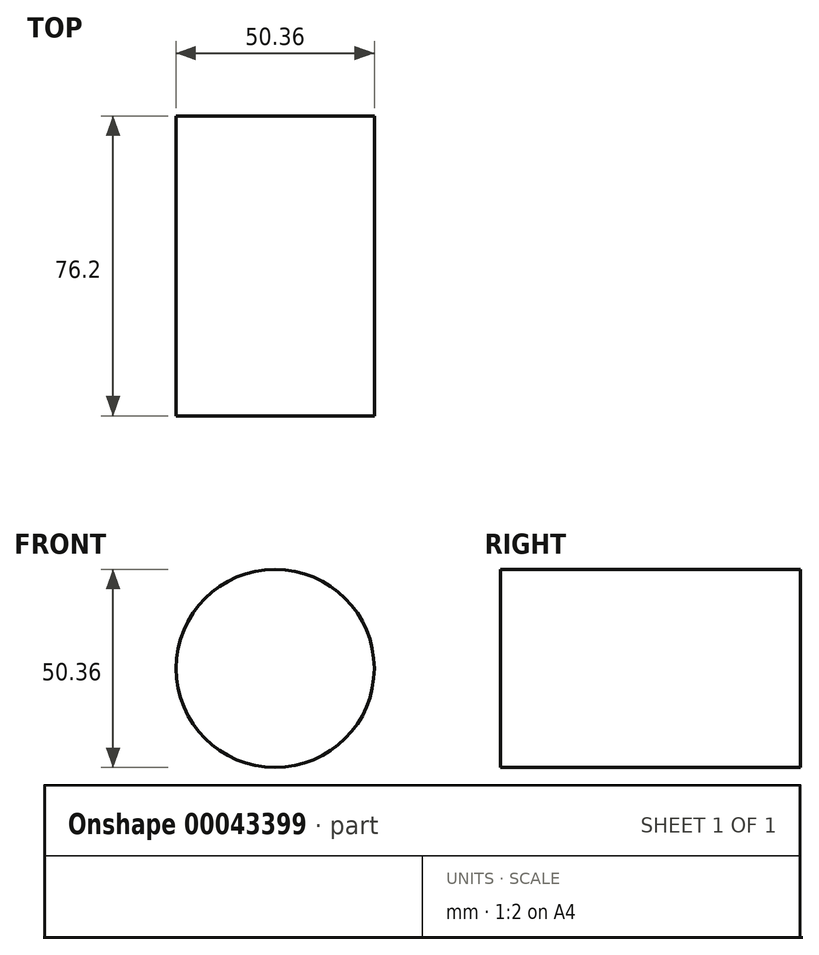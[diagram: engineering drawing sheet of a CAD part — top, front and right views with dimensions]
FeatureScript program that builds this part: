
annotation { "Feature Type Name" : "Feature", "Feature Type Description" : "" }
export const myFeature = defineFeature(function(context is Context, id is Id, definition is map)
    precondition{}
    {
        {
            var Q0;
            Q0=qCreatedBy(makeId("Front.planeOp"),FACE);
            var sketch = newSketch(context, id + "F0", { "sketchPlane" : qUnion([Q0])});
            skCircle(sketch, "E0", {"center": v(0, 0) * mm, "radius": 25.18 * mm});
            skSolve(sketch);
        }
        {
            var Q0;
            Q0=sQuery(id+"F0.wireOp",EDGE,"E0");
            extrude(context, id + "F1", {"bodyType" : ToolBodyType.SURFACE, "surfaceEntities" : qUnion([Q0]), "depth" : 76.2 * mm});
        }
    });
